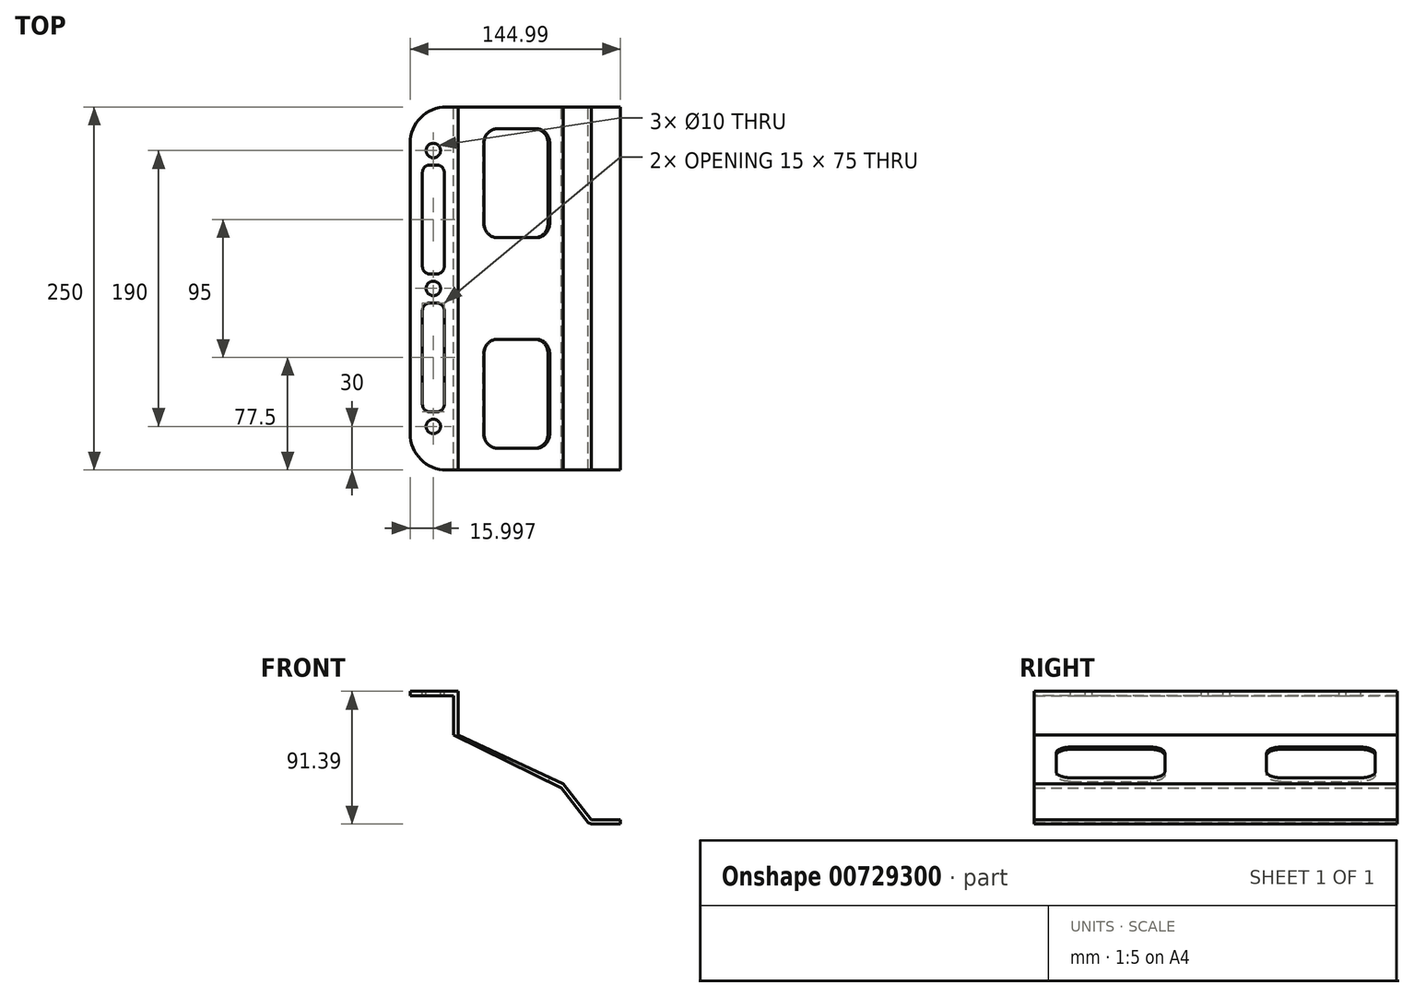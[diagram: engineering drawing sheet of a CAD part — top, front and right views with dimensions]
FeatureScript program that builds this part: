
annotation { "Feature Type Name" : "Feature", "Feature Type Description" : "" }
export const myFeature = defineFeature(function(context is Context, id is Id, definition is map)
    precondition{}
    {
        {
            var Q0;
            Q0=qCreatedBy(makeId("Front.planeOp"),FACE);
            var sketch = newSketch(context, id + "F0", { "sketchPlane" : qUnion([Q0])});
            skLineSegment(sketch, "E0.bottom", {"start": v(-77.15, 41.18) * mm, "end": v(-47.15, 41.18) * mm});
            skLineSegment(sketch, "E0.top", {"start": v(-77.15, 38.18) * mm, "end": v(-47.15, 38.18) * mm});
            skLineSegment(sketch, "E0.left", {"start": v(-77.15, 41.18) * mm, "end": v(-77.15, 38.18) * mm});
            skLineSegment(sketch, "E1.bottom", {"start": v(-47.15, 41.18) * mm, "end": v(-44.15, 41.18) * mm});
            skLineSegment(sketch, "E1.right", {"start": v(-44.15, 41.18) * mm, "end": v(-44.15, 11.18) * mm});
            skLineSegment(sketch, "E2", {"start": v(-44.15, 11.18) * mm, "end": v(28.35, -22.62) * mm});
            skLineSegment(sketch, "E3", {"start": v(27.08, -25.34) * mm, "end": v(-47.15, 11.18) * mm});
            skLineSegment(sketch, "E4", {"start": v(27.08, -25.34) * mm, "end": v(45.47, -49.05) * mm});
            skLineSegment(sketch, "E5", {"start": v(47.84, -47.21) * mm, "end": v(28.35, -22.62) * mm});
            skLineSegment(sketch, "E6", {"start": v(47.84, -47.21) * mm, "end": v(67.84, -47.21) * mm});
            skLineSegment(sketch, "E7", {"start": v(67.84, -47.21) * mm, "end": v(67.84, -50.21) * mm});
            skLineSegment(sketch, "E8", {"start": v(67.84, -50.21) * mm, "end": v(47.84, -50.21) * mm});
            skLineSegment(sketch, "E9", {"start": v(47.84, -50.21) * mm, "end": v(45.47, -49.05) * mm});
            skLineSegment(sketch, "E10", {"start": v(-47.15, 38.18) * mm, "end": v(-47.15, 11.18) * mm});
            skSolve(sketch);
        }
        {
            var Q0;
            Q0=makeQuery(id+"F0.imprint","IMPRINT",FACE,{"disambiguationData":[TD([[makeQuery(id+"F0.imprint","IMPRINT",EDGE,{"derivedFrom":sQuery(id+"F0.wireOp",EDGE,"E0.bottom")}),-1.0]])]});
            extrude(context, id + "F1", {"entities" : qUnion([Q0]), "depth" : 250 * mm, "offsetDistance" : 25 * mm});
        }
        {
            var Q0;
            Q0=makeQuery(id+"F1.opExtrude","SWEPT_FACE",FACE,{"disambiguationData":[OSD([sQuery(id+"F0.wireOp",EDGE,"E0.bottom"),sQuery(id+"F0.wireOp",EDGE,"E1.bottom")])]});
            var sketch = newSketch(context, id + "F2", { "sketchPlane" : qUnion([Q0])});
            skCircle(sketch, "E11", {"center": v(-61.15, -30) * mm, "radius": 5 * mm});
            skCircle(sketch, "E12", {"center": v(-61.15, -125) * mm, "radius": 5 * mm});
            skCircle(sketch, "E13", {"center": v(-61.15, -220) * mm, "radius": 5 * mm});
            skSolve(sketch);
        }
        {
            var Q0;
            Q0=makeQuery(id+"F2.imprint","IMPRINT",FACE,{"disambiguationData":[TD([[makeQuery(id+"F2.imprint","IMPRINT",EDGE,{"derivedFrom":sQuery(id+"F2.wireOp",EDGE,"E11")}),1.0]])]});
            var Q1;
            Q1=makeQuery(id+"F2.imprint","IMPRINT",FACE,{"disambiguationData":[TD([[makeQuery(id+"F2.imprint","IMPRINT",EDGE,{"derivedFrom":sQuery(id+"F2.wireOp",EDGE,"E12")}),1.0]])]});
            var Q2;
            Q2=makeQuery(id+"F2.imprint","IMPRINT",FACE,{"disambiguationData":[TD([[makeQuery(id+"F2.imprint","IMPRINT",EDGE,{"derivedFrom":sQuery(id+"F2.wireOp",EDGE,"E13")}),1.0]])]});
            extrude(context, id + "F3", {"entities" : qUnion([Q0, Q1, Q2]), "operationType" : NewBodyOperationType.REMOVE, "oppositeDirection" : true, "depth" : 25 * mm, "offsetDistance" : 25 * mm});
        }
        {
            var Q0;
            Q0=makeQuery(id+"F1.opExtrude","SWEPT_FACE",FACE,{"disambiguationData":[OSD([sQuery(id+"F0.wireOp",EDGE,"E0.bottom"),sQuery(id+"F0.wireOp",EDGE,"E1.bottom")])]});
            var sketch = newSketch(context, id + "F4", { "sketchPlane" : qUnion([Q0])});
            skLineSegment(sketch, "E14", {"start": v(-44.15, 0) * mm, "end": v(-52.15, 0) * mm});
            skLineSegment(sketch, "E15", {"start": v(-77.15, -25) * mm, "end": v(-77.15, -25) * mm});
            skPoint(sketch, "E16.visualSharp", {"position": v(-77.15, 0) * mm});
            skArc(sketch, "E16.filletArc", {"start": v(-52.15, 0) * mm, "mid": v(-69.83, -7.32) * mm, "end": v(-77.15, -25) * mm});
            skLineSegment(sketch, "E17", {"start": v(-44.15, -250) * mm, "end": v(-52.15, -250) * mm});
            skLineSegment(sketch, "E18", {"start": v(-77.15, -225) * mm, "end": v(-77.15, -225) * mm});
            skPoint(sketch, "E19.visualSharp", {"position": v(-77.15, -250) * mm});
            skArc(sketch, "E19.filletArc", {"start": v(-77.15, -225) * mm, "mid": v(-69.83, -242.68) * mm, "end": v(-52.15, -250) * mm});
            skSolve(sketch);
        }
        {
            var Q0;
            {var subQ0=sQuery(id+"F4.wireOp",EDGE,"E16.filletArc");Q0=makeQuery(id+"F4.imprint","IMPRINT",FACE,{"disambiguationData":[TD([[makeQuery(id+"F4.imprint","IMPRINT",EDGE,{"derivedFrom":subQ0}),-1.0]])]});}
            var Q1;
            {var subQ0=sQuery(id+"F4.wireOp",EDGE,"E19.filletArc");Q1=makeQuery(id+"F4.imprint","IMPRINT",FACE,{"disambiguationData":[TD([[makeQuery(id+"F4.imprint","IMPRINT",EDGE,{"derivedFrom":subQ0}),-1.0]])]});}
            extrude(context, id + "F5", {"entities" : qUnion([Q0, Q1]), "operationType" : NewBodyOperationType.REMOVE, "oppositeDirection" : true, "depth" : 25 * mm, "offsetDistance" : 25 * mm});
        }
        {
            var Q0;
            Q0=makeQuery(id+"F1.opExtrude","SWEPT_FACE",FACE,{"disambiguationData":[OSD([sQuery(id+"F0.wireOp",EDGE,"E0.bottom"),sQuery(id+"F0.wireOp",EDGE,"E1.bottom")])]});
            var sketch = newSketch(context, id + "F6", { "sketchPlane" : qUnion([Q0])});
            skLineSegment(sketch, "E20.bottom", {"start": v(-63.65, -40) * mm, "end": v(-58.65, -40) * mm});
            skLineSegment(sketch, "E20.top", {"start": v(-63.65, -115) * mm, "end": v(-58.65, -115) * mm});
            skLineSegment(sketch, "E20.left", {"start": v(-68.65, -45) * mm, "end": v(-68.65, -110) * mm});
            skLineSegment(sketch, "E20.right", {"start": v(-53.65, -45) * mm, "end": v(-53.65, -110) * mm});
            skPoint(sketch, "E21.visualSharp", {"position": v(-68.65, -40) * mm});
            skArc(sketch, "E21.filletArc", {"start": v(-63.65, -40) * mm, "mid": v(-67.19, -41.46) * mm, "end": v(-68.65, -45) * mm});
            skPoint(sketch, "E22.visualSharp", {"position": v(-53.65, -40) * mm});
            skArc(sketch, "E22.filletArc", {"start": v(-53.65, -45) * mm, "mid": v(-55.12, -41.46) * mm, "end": v(-58.65, -40) * mm});
            skPoint(sketch, "E23.visualSharp", {"position": v(-68.65, -115) * mm});
            skArc(sketch, "E23.filletArc", {"start": v(-68.65, -110) * mm, "mid": v(-67.19, -113.54) * mm, "end": v(-63.65, -115) * mm});
            skPoint(sketch, "E24.visualSharp", {"position": v(-53.65, -115) * mm});
            skArc(sketch, "E24.filletArc", {"start": v(-58.65, -115) * mm, "mid": v(-55.12, -113.54) * mm, "end": v(-53.65, -110) * mm});
            skLineSegment(sketch, "E25.bottom", {"start": v(-63.65, -135) * mm, "end": v(-58.65, -135) * mm});
            skLineSegment(sketch, "E25.top", {"start": v(-63.65, -210) * mm, "end": v(-58.65, -210) * mm});
            skLineSegment(sketch, "E25.left", {"start": v(-68.65, -140) * mm, "end": v(-68.65, -205) * mm});
            skLineSegment(sketch, "E25.right", {"start": v(-53.65, -140) * mm, "end": v(-53.65, -205) * mm});
            skPoint(sketch, "E26.visualSharp", {"position": v(-68.65, -135) * mm});
            skArc(sketch, "E26.filletArc", {"start": v(-63.65, -135) * mm, "mid": v(-67.19, -136.46) * mm, "end": v(-68.65, -140) * mm});
            skPoint(sketch, "E27.visualSharp", {"position": v(-53.65, -135) * mm});
            skArc(sketch, "E27.filletArc", {"start": v(-53.65, -140) * mm, "mid": v(-55.12, -136.46) * mm, "end": v(-58.65, -135) * mm});
            skPoint(sketch, "E28.visualSharp", {"position": v(-68.65, -210) * mm});
            skArc(sketch, "E28.filletArc", {"start": v(-68.65, -205) * mm, "mid": v(-67.19, -208.54) * mm, "end": v(-63.65, -210) * mm});
            skPoint(sketch, "E29.visualSharp", {"position": v(-53.65, -210) * mm});
            skArc(sketch, "E29.filletArc", {"start": v(-58.65, -210) * mm, "mid": v(-55.12, -208.54) * mm, "end": v(-53.65, -205) * mm});
            skSolve(sketch);
        }
        {
            var Q0;
            Q0=makeQuery(id+"F6.imprint","IMPRINT",FACE,{"disambiguationData":[TD([[makeQuery(id+"F6.imprint","IMPRINT",EDGE,{"derivedFrom":sQuery(id+"F6.wireOp",EDGE,"E20.bottom")}),-1.0]])]});
            var Q1;
            Q1=makeQuery(id+"F6.imprint","IMPRINT",FACE,{"disambiguationData":[TD([[makeQuery(id+"F6.imprint","IMPRINT",EDGE,{"derivedFrom":sQuery(id+"F6.wireOp",EDGE,"E25.bottom")}),-1.0]])]});
            extrude(context, id + "F7", {"entities" : qUnion([Q0, Q1]), "operationType" : NewBodyOperationType.REMOVE, "oppositeDirection" : true, "depth" : 25 * mm, "offsetDistance" : 25 * mm});
        }
        {
            var Q0;
            Q0=makeQuery(id+"F1.opExtrude","SWEPT_FACE",FACE,{"disambiguationData":[OSD([sQuery(id+"F0.wireOp",EDGE,"E2")])]});
            cPlane(context, id + "F8", {"entities" : qUnion([Q0]), "cplaneType" : CPlaneType.OFFSET, "offset" : 25 * mm, "width" : 150 * mm, "height" : 150 * mm});
        }
        {
            var Q0;
            Q0=qCreatedBy(id+"F8.planeOp",FACE);
            var sketch = newSketch(context, id + "F9", { "sketchPlane" : qUnion([Q0])});
            skLineSegment(sketch, "E30.bottom", {"start": v(-15, -15) * mm, "end": v(15, -15) * mm});
            skLineSegment(sketch, "E30.top", {"start": v(-15, -90) * mm, "end": v(15, -90) * mm});
            skLineSegment(sketch, "E30.left", {"start": v(-25, -25) * mm, "end": v(-25, -80) * mm});
            skLineSegment(sketch, "E30.right", {"start": v(25, -25) * mm, "end": v(25, -80) * mm});
            skLineSegment(sketch, "E31.bottom", {"start": v(-15, -160) * mm, "end": v(15, -160) * mm});
            skLineSegment(sketch, "E31.top", {"start": v(-15, -235) * mm, "end": v(15, -235) * mm});
            skLineSegment(sketch, "E31.left", {"start": v(-25, -170) * mm, "end": v(-25, -225) * mm});
            skLineSegment(sketch, "E31.right", {"start": v(25, -170) * mm, "end": v(25, -225) * mm});
            skPoint(sketch, "E32.visualSharp", {"position": v(-25, -15) * mm});
            skArc(sketch, "E32.filletArc", {"start": v(-15, -15) * mm, "mid": v(-22.07, -17.93) * mm, "end": v(-25, -25) * mm});
            skPoint(sketch, "E33.visualSharp", {"position": v(25, -15) * mm});
            skArc(sketch, "E33.filletArc", {"start": v(25, -25) * mm, "mid": v(22.07, -17.93) * mm, "end": v(15, -15) * mm});
            skPoint(sketch, "E34.visualSharp", {"position": v(25, -90) * mm});
            skArc(sketch, "E34.filletArc", {"start": v(15, -90) * mm, "mid": v(22.07, -87.07) * mm, "end": v(25, -80) * mm});
            skPoint(sketch, "E35.visualSharp", {"position": v(-25, -90) * mm});
            skArc(sketch, "E35.filletArc", {"start": v(-25, -80) * mm, "mid": v(-22.07, -87.07) * mm, "end": v(-15, -90) * mm});
            skPoint(sketch, "E36.visualSharp", {"position": v(-25, -160) * mm});
            skArc(sketch, "E36.filletArc", {"start": v(-15, -160) * mm, "mid": v(-22.07, -162.93) * mm, "end": v(-25, -170) * mm});
            skPoint(sketch, "E37.visualSharp", {"position": v(-25, -235) * mm});
            skArc(sketch, "E37.filletArc", {"start": v(-25, -225) * mm, "mid": v(-22.07, -232.07) * mm, "end": v(-15, -235) * mm});
            skPoint(sketch, "E38.visualSharp", {"position": v(25, -160) * mm});
            skArc(sketch, "E38.filletArc", {"start": v(25, -170) * mm, "mid": v(22.07, -162.93) * mm, "end": v(15, -160) * mm});
            skPoint(sketch, "E39.visualSharp", {"position": v(25, -235) * mm});
            skArc(sketch, "E39.filletArc", {"start": v(15, -235) * mm, "mid": v(22.07, -232.07) * mm, "end": v(25, -225) * mm});
            skSolve(sketch);
        }
        {
            var Q0;
            Q0=makeQuery(id+"F9.imprint","IMPRINT",FACE,{"disambiguationData":[TD([[makeQuery(id+"F9.imprint","IMPRINT",EDGE,{"derivedFrom":sQuery(id+"F9.wireOp",EDGE,"E30.bottom")}),-1.0]])]});
            var Q1;
            Q1=makeQuery(id+"F9.imprint","IMPRINT",FACE,{"disambiguationData":[TD([[makeQuery(id+"F9.imprint","IMPRINT",EDGE,{"derivedFrom":sQuery(id+"F9.wireOp",EDGE,"E31.bottom")}),-1.0]])]});
            extrude(context, id + "F10", {"entities" : qUnion([Q0, Q1]), "operationType" : NewBodyOperationType.REMOVE, "oppositeDirection" : true, "depth" : 100 * mm, "offsetDistance" : 25 * mm});
        }
    });
